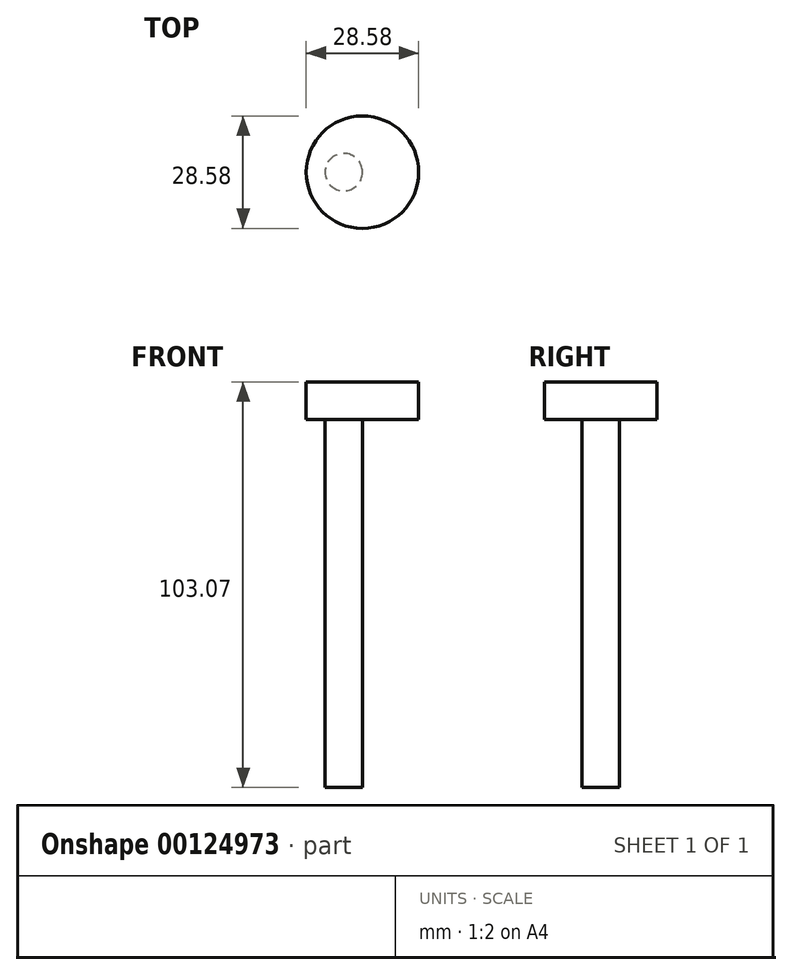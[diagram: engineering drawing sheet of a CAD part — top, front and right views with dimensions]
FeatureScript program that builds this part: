
annotation { "Feature Type Name" : "Feature", "Feature Type Description" : "" }
export const myFeature = defineFeature(function(context is Context, id is Id, definition is map)
    precondition{}
    {
        {
            var Q0;
            Q0=qCreatedBy(makeId("Top.planeOp"),FACE);
            var sketch = newSketch(context, id + "F0", { "sketchPlane" : qUnion([Q0])});
            skCircle(sketch, "E0", {"center": v(-7.3, -2.12) * mm, "radius": 4.76 * mm});
            skSolve(sketch);
        }
        {
            var Q0;
            Q0 = qSketchRegion(id + "F0", true);
            extrude(context, id + "F1", {"entities" : qUnion([Q0]), "depth" : 80.85 * mm});
        }
        {
            var Q0;
            Q0=makeQuery(id+"F1.opExtrude","CAP_FACE",FACE,{"disambiguationData":[OSD([sQuery(id+"F0.wireOp",EDGE,"E0")])],"isStart":false});
            var sketch = newSketch(context, id + "F2", { "sketchPlane" : qUnion([Q0])});
            skCircle(sketch, "E1", {"center": v(-2.53, -2.12) * mm, "radius": 14.29 * mm});
            skSolve(sketch);
        }
        {
            var Q0;
            Q0 = qSketchRegion(id + "F2", true);
            extrude(context, id + "F3", {"entities" : qUnion([Q0]), "operationType" : NewBodyOperationType.ADD, "depth" : 9.52 * mm});
        }
        {
            var Q0;
            Q0 = qSketchRegion(id + "F0", true);
            extrude(context, id + "F4", {"entities" : qUnion([Q0]), "operationType" : NewBodyOperationType.ADD, "oppositeDirection" : true, "depth" : 12.7 * mm});
        }
    });
